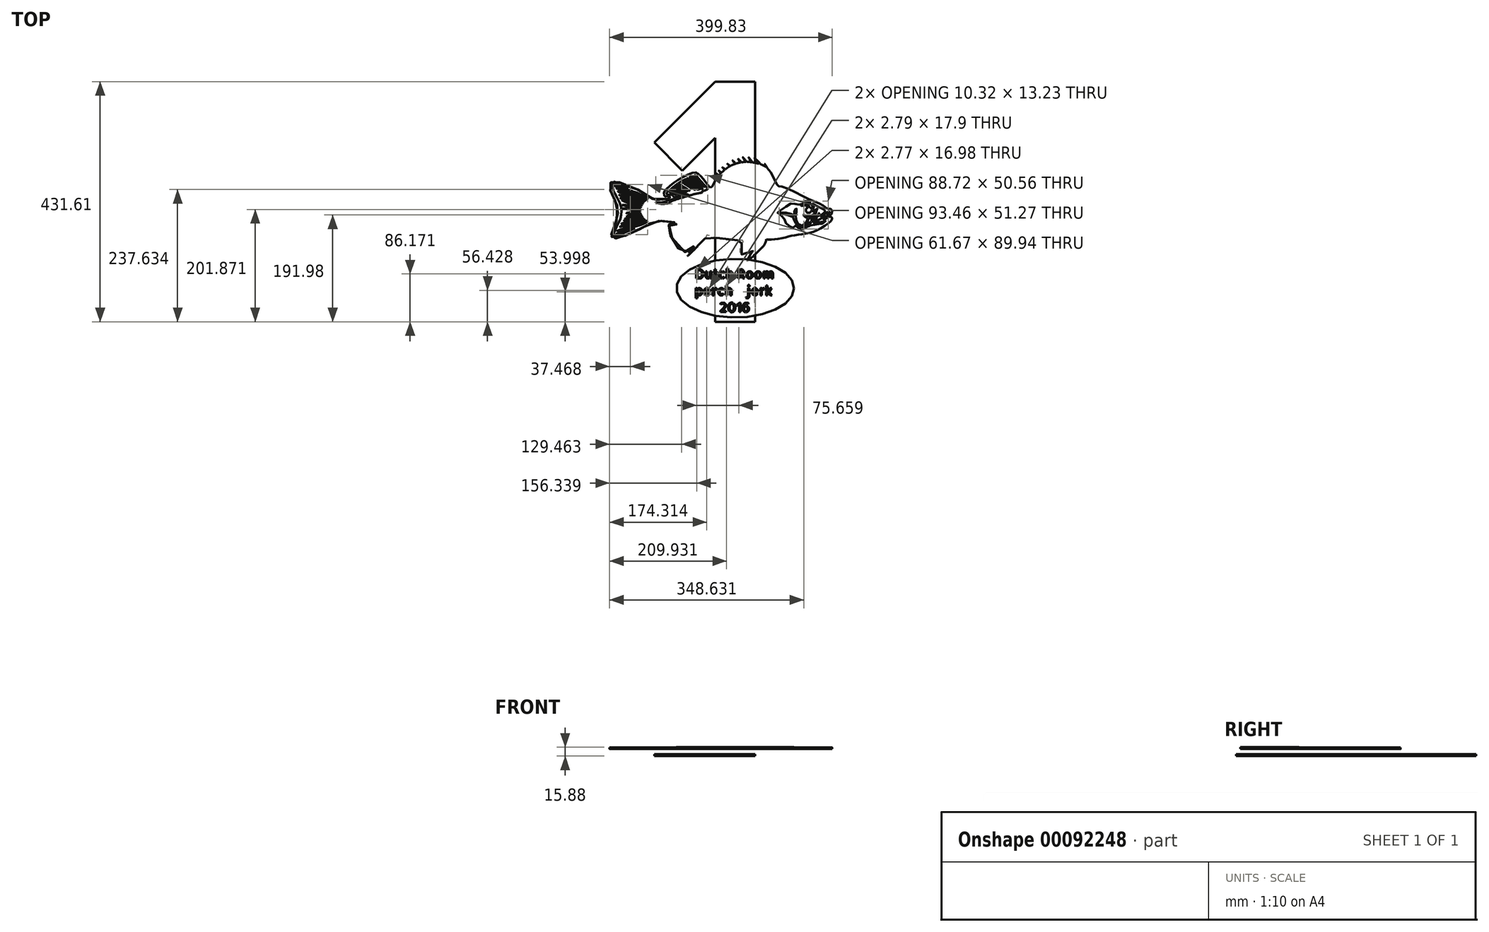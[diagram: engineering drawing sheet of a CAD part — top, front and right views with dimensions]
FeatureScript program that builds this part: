
annotation { "Feature Type Name" : "Feature", "Feature Type Description" : "" }
export const myFeature = defineFeature(function(context is Context, id is Id, definition is map)
    precondition{}
    {
        {
            var Q0;
            Q0=qCreatedBy(makeId("Top.planeOp"),FACE);
            var sketch = newSketch(context, id + "F0", { "sketchPlane" : qUnion([Q0])});
            skFitSpline(sketch, "E0", {"points": [v(176.52, -244.27) * mm, v(181.2, -242.71) * mm, v(184.05, -245.3) * mm, v(182.5, -249.99) * mm, v(166.12, -262.72) * mm, v(147.15, -271.03) * mm, v(127.92, -274.93) * mm, v(113.37, -276.75) * mm, v(102.2, -279.6) * mm, v(84.87, -283.22) * mm, v(72.52, -283.98) * mm, v(66.52, -283.55) * mm, v(66.52, -283.55) * mm], "startDerivative": vector(81.4, 45.99) * mm, "endDerivative": vector(4.56, -0.01) * mm});
            skFitSpline(sketch, "E1", {"points": [v(66.52, -283.55) * mm, v(62.28, -294) * mm, v(51.55, -305.13) * mm, v(31.43, -322.92) * mm, v(42.66, -306.88) * mm, v(44.26, -305.13) * mm, v(43.38, -303.53) * mm, v(41.05, -304.99) * mm, v(35.95, -308.05) * mm, v(30.4, -310.53) * mm, v(21.22, -310.38) * mm, v(19.47, -302.5) * mm, v(20.2, -296.53) * mm, v(22.97, -289.82) * mm, v(25.3, -288.21) * mm, v(25.16, -286.03) * mm, v(22.82, -285.44) * mm, v(2.55, -285.3) * mm, v(-21.84, -281.67) * mm, v(-40.3, -275.97) * mm, v(-41.5, -278) * mm, v(-45.18, -283.55) * mm, v(-56.84, -295.63) * mm, v(-75.03, -313) * mm, v(-64.28, -298.02) * mm, v(-63.92, -296.46) * mm, v(-65.39, -296.55) * mm, v(-71.63, -302.52) * mm, v(-78.16, -306.01) * mm, v(-86.6, -304.73) * mm, v(-102.6, -282.27) * mm, v(-109.19, -265.88) * mm, v(-108.93, -258.69) * mm, v(-107.97, -256.6) * mm, v(-94.27, -256.52) * mm, v(-93.4, -254.44) * mm, v(-105.8, -252.01) * mm, v(-114.2, -250.8) * mm, v(-131.46, -251.01) * mm, v(-145, -256.26) * mm, v(-161.4, -265.22) * mm, v(-180.4, -273.96) * mm, v(-199.85, -281.39) * mm, v(-209.53, -281.24) * mm, v(-211.93, -278.9) * mm, v(-211.33, -270.32) * mm, v(-201.79, -247.1) * mm, v(-200.61, -241.8) * mm, v(-200.76, -226.33) * mm, v(-209.59, -206.64) * mm, v(-213.82, -195.7) * mm, v(-215.13, -185.5) * mm, v(-212.5, -180.54) * mm, v(-206.96, -179.8) * mm, v(-177.94, -187.83) * mm, v(-144.11, -206.64) * mm, v(-140.17, -209.7) * mm, v(-133.8, -212.3) * mm, v(-127, -212.85) * mm, v(-113.58, -210.83) * mm], "startDerivative": vector(-201.77, -623.7) * mm, "endDerivative": vector(821.63, 283.32) * mm});
            skFitSpline(sketch, "E2", {"points": [v(-113.58, -210.83) * mm, v(-106.81, -209.28) * mm, v(-107.23, -207.02) * mm, v(-111.66, -206.3) * mm, v(-116.5, -206.5) * mm, v(-117.64, -203.3) * mm, v(-117.74, -199.7) * mm, v(-115.89, -196.3) * mm, v(-103.3, -184.43) * mm, v(-82.53, -171.12) * mm, v(-62.72, -163.46) * mm, v(-57.17, -165.44) * mm, v(-45.04, -177.42) * mm, v(-35.04, -190.1) * mm, v(-31.64, -189.07) * mm, v(-25.86, -178.35) * mm, v(-10.7, -160.5) * mm, v(5.27, -149.84) * mm, v(21.47, -145.14) * mm, v(35.7, -144.53) * mm, v(54.05, -148.13) * mm, v(67.01, -154.67) * mm, v(78, -169.98) * mm, v(87.26, -187.63) * mm, v(89.22, -188.14) * mm, v(99.74, -190.52) * mm, v(131.4, -205.68) * mm, v(139.48, -210.3) * mm, v(141.8, -211.3) * mm, v(145.18, -212.3) * mm, v(160.7, -218.96) * mm, v(162.02, -219.5) * mm, v(172.6, -225.45) * mm, v(175.46, -228.46) * mm, v(178.32, -228.46) * mm, v(181.2, -228.7) * mm, v(183.34, -230.31) * mm, v(184.58, -234.1) * mm, v(183.03, -238.58) * mm, v(176.52, -242.71) * mm, v(168.66, -248.55) * mm, v(176.52, -244.27) * mm], "startDerivative": vector(420.31, 27.33) * mm, "endDerivative": vector(492.44, 290.81) * mm});
            skFitSpline(sketch, "E3", {"points": [v(67.9, -155.44) * mm, v(63.55, -148.16) * mm, v(66.03, -153.88) * mm], "startDerivative": vector(-11.62, 20.57) * mm, "endDerivative": vector(8.42, -18.44) * mm});
            skFitSpline(sketch, "E4", {"points": [v(56.05, -148.79) * mm, v(45.15, -137.39) * mm, v(52.55, -147.68) * mm], "startDerivative": vector(-30.23, 33.1) * mm, "endDerivative": vector(24.2, -32.08) * mm});
            skFitSpline(sketch, "E5", {"points": [v(41.73, -145.27) * mm, v(34.48, -136.4) * mm, v(39.55, -144.95) * mm], "startDerivative": vector(-20.35, 26.15) * mm, "endDerivative": vector(16.4, -26.19) * mm});
            skFitSpline(sketch, "E6", {"points": [v(31.23, -144.33) * mm, v(23.93, -136.07) * mm, v(29.46, -144.35) * mm], "startDerivative": vector(-20.79, 24.67) * mm, "endDerivative": vector(17.59, -25.1) * mm});
            skFitSpline(sketch, "E7", {"points": [v(21.47, -145.14) * mm, v(15.64, -139.28) * mm, v(19.95, -145.4) * mm, v(19.97, -145.4) * mm], "startDerivative": vector(-18.77, 20.63) * mm, "endDerivative": vector(0.36, 0.58) * mm});
            skFitSpline(sketch, "E8", {"points": [v(11.32, -147.55) * mm, v(5.77, -141.8) * mm, v(10.2, -147.92) * mm], "startDerivative": vector(-16.02, 17.44) * mm, "endDerivative": vector(13.93, -18.32) * mm});
            skFitSpline(sketch, "E9", {"points": [v(0.95, -152.01) * mm, v(-3.57, -147.89) * mm, v(0, -152.56) * mm], "startDerivative": vector(-13.03, 12.6) * mm, "endDerivative": vector(11.2, -13.78) * mm});
            skFitSpline(sketch, "E10", {"points": [v(-7.5, -157.78) * mm, v(-12.5, -154.25) * mm, v(-8.76, -158.82) * mm], "startDerivative": vector(-14.36, 11.14) * mm, "endDerivative": vector(11.94, -13.32) * mm});
            skFitSpline(sketch, "E11", {"points": [v(-14.39, -163.98) * mm, v(-19.08, -160.13) * mm, v(-15.48, -165.1) * mm], "startDerivative": vector(-13.57, 12.16) * mm, "endDerivative": vector(11.37, -14.38) * mm});
            skFitSpline(sketch, "E12", {"points": [v(-19.2, -169.16) * mm, v(-23.41, -165.03) * mm, v(-20.42, -170.62) * mm], "startDerivative": vector(-12.18, 13.25) * mm, "endDerivative": vector(9.62, -15.99) * mm});
            skFitSpline(sketch, "E13", {"points": [v(-24.52, -176.18) * mm, v(-27.73, -174.74) * mm, v(-25.1, -177.07) * mm, v(-25.16, -177.17) * mm], "startDerivative": vector(-11.42, 5.96) * mm, "endDerivative": vector(-1.56, -0.68) * mm});
            skSolve(sketch);
        }
        {
            var Q0;
            Q0 = qSketchRegion(id + "F0", true);
            extrude(context, id + "F1", {"entities" : qUnion([Q0]), "depth" : 2.54 * mm});
        }
        {
            var Q0;
            Q0=qCreatedBy(makeId("Top.planeOp"),FACE);
            var sketch = newSketch(context, id + "F2", { "sketchPlane" : qUnion([Q0])});
            skFitSpline(sketch, "E14", {"points": [v(-142.26, -213.51) * mm, v(-147.05, -215.6) * mm, v(-152.07, -221.24) * mm, v(-154.16, -227.5) * mm, v(-155.38, -233.26) * mm, v(-153.8, -240.25) * mm, v(-149.87, -244.42) * mm, v(-145.45, -248.59) * mm, v(-143.73, -249.81) * mm, v(-139.32, -247.48) * mm, v(-131.23, -244.54) * mm, v(-118.23, -243.56) * mm, v(-105.72, -246.62) * mm, v(-93.21, -251.04) * mm, v(-77.15, -255.2) * mm, v(-72, -257.17) * mm, v(-75.55, -258.4) * mm, v(-61.45, -263.67) * mm, v(-42.32, -270.17) * mm, v(-22.11, -275.38) * mm, v(-3.6, -278.44) * mm, v(8.22, -280.05) * mm, v(24.12, -281.8) * mm, v(29.95, -281.94) * mm, v(30.82, -280.2) * mm, v(41.76, -276.26) * mm, v(55.9, -276.84) * mm, v(59.12, -278.59) * mm, v(47.74, -279.32) * mm, v(37.53, -281.94) * mm, v(32, -286.32) * mm, v(27.18, -292.15) * mm, v(27.32, -293.6) * mm, v(44.82, -281.8) * mm, v(46.43, -282.53) * mm, v(24.55, -298.57) * mm, v(23.82, -300.76) * mm, v(26.01, -301.05) * mm, v(33.16, -294.92) * mm, v(44.39, -286.6) * mm, v(50.8, -282.38) * mm, v(51.53, -284.13) * mm, v(48.03, -287.2) * mm, v(39.43, -293.46) * mm, v(30.53, -300.46) * mm, v(25.57, -304.55) * mm, v(31.84, -301.78) * mm, v(39.72, -295.8) * mm, v(49.64, -288.5) * mm, v(55.76, -283.84) * mm, v(56.34, -285.44) * mm, v(31.12, -304.4) * mm, v(31.7, -305.57) * mm, v(34.47, -304.55) * mm, v(54.3, -289.53) * mm, v(57.95, -285) * mm, v(57.66, -288.8) * mm, v(57.37, -291.13) * mm, v(60.43, -286.76) * mm, v(63.2, -281.36) * mm, v(64.07, -278.59) * mm, v(66.55, -279.32) * mm, v(85.51, -277.71) * mm, v(100.67, -274.05) * mm, v(108.48, -272.49) * mm, v(108.83, -270.75) * mm, v(106.22, -270.4) * mm, v(96.86, -263.47) * mm, v(90.62, -253.93) * mm, v(82.46, -243.87) * mm, v(73.62, -237.45) * mm, v(73.97, -236.07) * mm, v(80.9, -229.65) * mm, v(101.57, -216.36) * mm, v(113.84, -210.8) * mm, v(117.3, -212.43) * mm, v(122.4, -212.9) * mm, v(124.25, -210.8) * mm, v(128.88, -210.58) * mm, v(128.88, -210.58) * mm], "startDerivative": vector(-461.18, -146.1) * mm, "endDerivative": vector(-122.05, -8.96) * mm});
            skFitSpline(sketch, "E15", {"points": [v(-142.26, -213.51) * mm, v(-136.94, -215.88) * mm, v(-129.76, -217.43) * mm, v(-121.5, -217.04) * mm, v(-111.76, -214.5) * mm, v(-100.55, -210.94) * mm, v(-94.68, -209.16) * mm, v(-92.52, -208.55) * mm, v(-84.7, -206.4) * mm, v(-73.42, -203.91) * mm, v(-65.34, -202.68) * mm, v(-48.61, -199.53) * mm, v(-40.34, -198.26) * mm, v(-25.45, -194.95) * mm, v(-7.05, -192.13) * mm, v(5.6, -190.67) * mm, v(19.33, -189.7) * mm, v(36.58, -189.54) * mm, v(56.32, -187.87) * mm, v(78.33, -190.04) * mm, v(91.1, -193.47) * mm, v(101.09, -197.29) * mm, v(116.95, -203.8) * mm, v(128.88, -210.58) * mm], "startDerivative": vector(164.66, -82.1) * mm, "endDerivative": vector(236.1, -141.25) * mm});
            skFitSpline(sketch, "E16", {"points": [v(113.84, -210.8) * mm, v(108.11, -206.07) * mm, v(89.62, -200.81) * mm, v(64.5, -197.7) * mm, v(25.96, -197.7) * mm, v(-2.85, -201.4) * mm, v(-37.1, -207.43) * mm, v(-58.04, -211.88) * mm, v(-81.65, -216.02) * mm, v(-109.12, -218.96) * mm, v(-126.3, -219.23) * mm, v(-132.51, -217.05) * mm, v(-132.6, -217.04) * mm], "startDerivative": vector(-86.44, 93.94) * mm, "endDerivative": vector(-9.69, 0.28) * mm});
            skFitSpline(sketch, "E17", {"points": [v(110.88, -211.42) * mm, v(106.7, -208.35) * mm, v(100.73, -206.42) * mm, v(88.23, -204.77) * mm, v(77.85, -203.66) * mm, v(63.6, -202.47) * mm, v(62.23, -204.58) * mm, v(56.17, -228.28) * mm, v(54.6, -244.82) * mm, v(51.4, -234.07) * mm, v(48.82, -221.85) * mm, v(48.08, -202.84) * mm, v(46.61, -202.93) * mm, v(24.2, -203.48) * mm, v(23.1, -203.94) * mm, v(19.15, -224.52) * mm, v(15.75, -254.28) * mm, v(11.06, -236.28) * mm, v(9.04, -220.2) * mm, v(8.4, -206.05) * mm, v(6.1, -205.87) * mm, v(-10.71, -208.17) * mm, v(-12, -209.73) * mm, v(-16.22, -234.8) * mm, v(-18.06, -259.1) * mm, v(-24.82, -241.93) * mm, v(-28.3, -219.22) * mm, v(-28.81, -211.06) * mm, v(-29.7, -211.13) * mm, v(-47.75, -215.43) * mm, v(-48.06, -216.13) * mm, v(-49.22, -236.21) * mm, v(-49.53, -251.9) * mm, v(-54.16, -238.07) * mm, v(-57.72, -222.54) * mm, v(-58.95, -217.29) * mm, v(-60.27, -217.52) * mm, v(-81.51, -220.15) * mm, v(-82.05, -221.46) * mm, v(-82.51, -236.83) * mm, v(-83.13, -248.57) * mm, v(-88.08, -232.97) * mm, v(-90.4, -221.92) * mm, v(-91.78, -221.85) * mm, v(-101.67, -223.24) * mm, v(-111.64, -223.31) * mm, v(-111.95, -224.16) * mm, v(-112.1, -234.6) * mm, v(-112.1, -240.46) * mm, v(-115.5, -233.05) * mm, v(-118.05, -223.62) * mm, v(-130.02, -220.84) * mm, v(-131.1, -220.38) * mm, v(-135.6, -216.32) * mm, v(-135.47, -216.36) * mm], "startDerivative": vector(-300.42, 251) * mm, "endDerivative": vector(93.72, -45.72) * mm});
            skFitSpline(sketch, "E18", {"points": [v(114.07, -272.25) * mm, v(112.54, -271.02) * mm, v(112.3, -269.19) * mm, v(110.77, -268.65) * mm, v(106.68, -268.35) * mm, v(100.75, -263.87) * mm, v(94.04, -253.38) * mm, v(86.64, -242.73) * mm, v(80.42, -237.52) * mm, v(79.5, -235.96) * mm, v(80.74, -234.33) * mm, v(91.08, -226.74) * mm, v(100.89, -220.78) * mm, v(108.9, -216.64) * mm, v(115.19, -214.67) * mm, v(118.42, -215.85) * mm, v(121.55, -217.02) * mm, v(124.4, -215.8) * mm, v(126.2, -212.84) * mm, v(129.09, -212.62) * mm, v(131.99, -213.61) * mm, v(132.6, -217.15) * mm, v(134.83, -215.7) * mm, v(138.68, -214.57) * mm, v(146.58, -217.76) * mm, v(157.66, -223.72) * mm, v(171.27, -231.95) * mm, v(171.47, -234.92) * mm, v(163.96, -240.97) * mm, v(164.51, -242.66) * mm, v(172.4, -237.44) * mm, v(177.17, -234.05) * mm, v(180.4, -234.75) * mm, v(177.65, -237.77) * mm, v(166.02, -245.76) * mm, v(153.23, -252.99) * mm, v(160.84, -252.94) * mm, v(169.34, -251.6) * mm, v(172.74, -251.02) * mm, v(167.8, -254.76) * mm, v(163.1, -256.48) * mm, v(155.54, -256.22) * mm, v(152.25, -257.37) * mm, v(145.11, -258.38) * mm, v(139.47, -261) * mm, v(133.94, -264.72) * mm, v(125.11, -265.22) * mm, v(122.47, -260.9) * mm, v(118.83, -258.43) * mm, v(114.86, -261.9) * mm, v(112.32, -263.71) * mm, v(105.55, -258.02) * mm, v(100.44, -253.03) * mm, v(98.75, -247.82) * mm, v(95.06, -242.4) * mm, v(87.19, -236.87) * mm, v(86.44, -235.25) * mm, v(93.42, -230.2) * mm, v(104.62, -223.1) * mm, v(113.26, -218.38) * mm, v(119.83, -221.1) * mm, v(124.77, -221.12) * mm, v(126.68, -219.6) * mm, v(132.7, -219.83) * mm, v(134.89, -215.98) * mm, v(134.87, -215.68) * mm], "startDerivative": vector(-231.95, 104.03) * mm, "endDerivative": vector(-1.9, 17.59) * mm});
            skFitSpline(sketch, "E19", {"points": [v(114.07, -272.25) * mm, v(114.93, -272.67) * mm, v(119.04, -271.33) * mm, v(128.15, -270.86) * mm, v(136.88, -269) * mm, v(150.03, -264.7) * mm, v(156.6, -261.53) * mm, v(160.18, -259.5) * mm, v(161.11, -258.14) * mm, v(157.26, -257.94) * mm, v(152.96, -259.12) * mm, v(146.58, -260.36) * mm, v(141.2, -262.76) * mm, v(136, -266.4) * mm, v(130.3, -267.74) * mm, v(124.31, -267.9) * mm, v(121.19, -264.25) * mm, v(119.46, -262.11) * mm, v(116.13, -265.4) * mm, v(111.7, -266.3) * mm, v(105.97, -262.09) * mm, v(99.28, -255.48) * mm, v(94.25, -246.72) * mm, v(89.25, -241.55) * mm, v(83.67, -237.6) * mm, v(84.09, -232.91) * mm], "startDerivative": vector(42.63, -35.7) * mm, "endDerivative": vector(113.94, 375.94) * mm});
            skFitSpline(sketch, "E20", {"points": [v(132.56, -217.1) * mm, v(131.6, -218.46) * mm, v(129.07, -218.1) * mm, v(123.9, -218.23) * mm, v(122.18, -218.96) * mm, v(119.76, -217.82) * mm, v(114.98, -217.06) * mm, v(108.79, -218.09) * mm, v(94.64, -226.9) * mm, v(83.97, -233.3) * mm], "startDerivative": vector(-6.58, -27.36) * mm, "endDerivative": vector(-52.9, -37.16) * mm});
            skLineSegment(sketch, "E21", {"start": v(134.89, -215.85) * mm, "end": v(134.83, -215.7) * mm});
            skFitSpline(sketch, "E22", {"points": [v(89.01, -236.2) * mm, v(100.1, -235.35) * mm, v(110.68, -238.2) * mm, v(116.19, -240.38) * mm, v(116.53, -233.6) * mm, v(117.93, -230.64) * mm, v(119.7, -227.07) * mm, v(120.96, -231.7) * mm, v(119.89, -235.19) * mm, v(119.49, -247.44) * mm, v(121.59, -253.51) * mm, v(126.76, -258.11) * mm, v(136.63, -257.82) * mm, v(144.56, -252.99) * mm, v(147.04, -251.16) * mm, v(145.47, -255.27) * mm, v(136.9, -260.6) * mm, v(126.26, -261.82) * mm, v(120.4, -256.5) * mm, v(116.06, -249.48) * mm, v(115.1, -244.9) * mm, v(108.08, -241.12) * mm, v(89.01, -236.2) * mm]});
            skFitSpline(sketch, "E23", {"points": [v(157.78, -228.5) * mm, v(154.47, -230.65) * mm, v(149.76, -230.13) * mm, v(140.29, -222.43) * mm, v(136.57, -220.9) * mm, v(131.99, -221.35) * mm, v(128.16, -222.52) * mm, v(130.12, -223.42) * mm, v(131.99, -223.1) * mm, v(136.14, -222.55) * mm, v(140.13, -225.75) * mm, v(145.4, -230.7) * mm, v(149.23, -232.79) * mm, v(152.45, -234.07) * mm, v(156.41, -231.85) * mm, v(157.78, -228.5) * mm]});
            skFitSpline(sketch, "E24", {"points": [v(151.33, -233.85) * mm, v(150.28, -234.18) * mm, v(149.56, -235.95) * mm, v(146.68, -238.41) * mm, v(142.24, -239.42) * mm, v(136.75, -238.8) * mm, v(133.5, -235.2) * mm, v(132.17, -230.35) * mm, v(132.9, -225.97) * mm, v(135.58, -222.47) * mm, v(135.58, -222.47) * mm], "startDerivative": vector(-20.32, -2.1) * mm, "endDerivative": vector(-2.43, -0.54) * mm});
            skFitSpline(sketch, "E25", {"points": [v(141.16, -226.87) * mm, v(140.03, -227.18) * mm, v(137.78, -228.86) * mm, v(137.78, -232.86) * mm, v(139.73, -235.52) * mm, v(144.64, -235.33) * mm, v(147.14, -231.74) * mm], "startDerivative": vector(-10.06, -2.2) * mm, "endDerivative": vector(9.28, 22.22) * mm});
            skFitSpline(sketch, "E26", {"points": [v(151.83, -238.53) * mm, v(148.99, -241.91) * mm, v(144.24, -245.3) * mm, v(138.46, -244.7) * mm, v(134.2, -241.7) * mm, v(132.9, -239.34) * mm, v(136.54, -240.92) * mm, v(139.8, -242.05) * mm, v(145.35, -242) * mm, v(148.24, -240.02) * mm, v(151.83, -238.53) * mm]});
            skFitSpline(sketch, "E27", {"points": [v(160.82, -236.26) * mm, v(159.79, -238.66) * mm, v(157.66, -240.24) * mm, v(153.8, -242.41) * mm, v(148.46, -244.91) * mm, v(147.27, -248.12) * mm, v(147.83, -249.95) * mm, v(148.52, -247.2) * mm, v(151.68, -245.02) * mm, v(158.31, -242.21) * mm, v(161.2, -240.38) * mm, v(160.82, -236.26) * mm]});
            skFitSpline(sketch, "E28", {"points": [v(148.96, -219.04) * mm, v(149.85, -220.95) * mm, v(151.94, -223.46) * mm, v(150.6, -223.62) * mm, v(148.3, -221.75) * mm, v(144.87, -220.21) * mm, v(141.04, -220.46) * mm, v(138.77, -218.1) * mm, v(143.68, -218.1) * mm, v(146.3, -217.61) * mm], "startDerivative": vector(5.22, -18.68) * mm, "endDerivative": vector(19.33, 6.7) * mm});
            skFitSpline(sketch, "E29", {"points": [v(138.77, -224.27) * mm, v(136.97, -224.53) * mm, v(134.9, -225.82) * mm, v(134.1, -229.7) * mm, v(135.2, -234.72) * mm, v(138.5, -237.13) * mm, v(143.91, -237.4) * mm, v(147.52, -236.36) * mm, v(148.35, -234.58) * mm, v(149.23, -232.79) * mm], "startDerivative": vector(-20.93, -1.63) * mm, "endDerivative": vector(11.28, 20.03) * mm});
            skFitSpline(sketch, "E30.0.0", {"points": [v(66.52, -283.55) * mm, v(66.52, -283.55) * mm, v(66.42, -283.55) * mm, v(74.1, -284.32) * mm, v(84.7, -283.6) * mm, v(102.41, -279.81) * mm, v(113.23, -276.26) * mm, v(128.3, -275.22) * mm, v(147.76, -271.61) * mm, v(165.7, -264.01) * mm, v(182.85, -251.2) * mm, v(184.98, -245.38) * mm, v(181.16, -241.65) * mm, v(178.13, -243.36) * mm, v(176.52, -244.27) * mm]});
            skFitSpline(sketch, "E30.0.1", {"points": [v(176.52, -244.27) * mm, v(172.56, -246.6) * mm, v(164.49, -251.37) * mm, v(177.06, -241.76) * mm, v(183.4, -239.52) * mm, v(185.1, -234.14) * mm, v(183.64, -230.17) * mm, v(181.27, -228.43) * mm, v(178.38, -228.33) * mm, v(174.9, -229.08) * mm, v(173.51, -224.74) * mm, v(161.63, -219.27) * mm, v(161.13, -219.21) * mm, v(144.96, -211.84) * mm, v(141.99, -211.46) * mm, v(138.96, -210.15) * mm, v(130.98, -205.12) * mm, v(100.96, -189.67) * mm, v(89.55, -187.92) * mm, v(86.36, -188.53) * mm, v(78.01, -168.4) * mm, v(68.21, -153.75) * mm, v(54.28, -147.55) * mm, v(35.6, -143.82) * mm, v(21.51, -144.63) * mm, v(4.44, -149.08) * mm, v(-11.16, -159.71) * mm, v(-26.53, -176.94) * mm, v(-30.53, -189.27) * mm, v(-36.2, -191.76) * mm, v(-44.45, -176.23) * mm, v(-56.8, -165.31) * mm, v(-62.88, -161.88) * mm, v(-84.09, -171.24) * mm, v(-102.65, -182.95) * mm, v(-115.87, -195.67) * mm, v(-118.07, -199.5) * mm, v(-117.66, -203.16) * mm, v(-117.16, -207.63) * mm, v(-111.64, -205.96) * mm, v(-106.9, -206.24) * mm, v(-105.93, -210.33) * mm, v(-110.6, -210.64) * mm, v(-113.58, -210.83) * mm]});
            skFitSpline(sketch, "E30.0.2", {"points": [v(-113.58, -210.83) * mm, v(-118.9, -212.67) * mm, v(-126.66, -212.92) * mm, v(-133.56, -212.81) * mm, v(-140.73, -209.79) * mm, v(-144.08, -205.9) * mm, v(-177.46, -185.5) * mm, v(-205.73, -179.4) * mm, v(-212.84, -179.67) * mm, v(-216.15, -185.72) * mm, v(-213.9, -196.33) * mm, v(-210.09, -206.96) * mm, v(-198.52, -225.17) * mm, v(-200.7, -242.08) * mm, v(-201.08, -246.91) * mm, v(-212.46, -269.82) * mm, v(-212.67, -278.83) * mm, v(-209.51, -282) * mm, v(-198.67, -282.4) * mm, v(-180.05, -273.65) * mm, v(-161.56, -265.8) * mm, v(-145.06, -256.06) * mm, v(-132.35, -249.8) * mm, v(-113.65, -250.47) * mm, v(-107.06, -252.21) * mm, v(-92.07, -252.92) * mm, v(-93.81, -258.37) * mm, v(-109.08, -255.08) * mm, v(-108.76, -259.03) * mm, v(-110.28, -267.02) * mm, v(-103, -282.17) * mm, v(-88.71, -306.96) * mm, v(-78.02, -306.53) * mm, v(-71.52, -303.33) * mm, v(-66.03, -296.1) * mm, v(-63.61, -296.31) * mm, v(-63.8, -298.28) * mm, v(-84.83, -324.13) * mm, v(-54.86, -293.49) * mm, v(-45.8, -284.73) * mm, v(-41.23, -278.42) * mm, v(-40.99, -273.87) * mm, v(-19.72, -283.8) * mm, v(0.59, -285.64) * mm, v(22.16, -285.4) * mm, v(25.4, -285.47) * mm, v(25.82, -288.8) * mm, v(22.14, -289.2) * mm, v(19.9, -296.97) * mm, v(19.38, -302) * mm, v(19.27, -312.7) * mm, v(30.96, -310.86) * mm, v(35.68, -308.13) * mm, v(40.93, -305.49) * mm, v(43.4, -302.59) * mm, v(44.7, -305.65) * mm, v(42.36, -306) * mm, v(21.33, -335.07) * mm, v(53.37, -302.82) * mm, v(62.66, -295.5) * mm, v(65.33, -287.24) * mm, v(66.52, -283.55) * mm]});
            skFitSpline(sketch, "E31", {"points": [v(-73.42, -203.91) * mm, v(-77.32, -202.4) * mm, v(-91.25, -205.23) * mm, v(-99.63, -207.85) * mm, v(-100.8, -205.74) * mm, v(-105.08, -203.47) * mm, v(-110.88, -203.23) * mm, v(-111.84, -203.08) * mm, v(-112.5, -201.81) * mm, v(-112.45, -199.8) * mm, v(-107.45, -194.7) * mm, v(-94.38, -184.27) * mm, v(-79.07, -175.46) * mm, v(-65.97, -169.49) * mm, v(-62.72, -168.43) * mm, v(-60.71, -168.53) * mm, v(-58.4, -170.64) * mm, v(-52.96, -177.03) * mm, v(-44.16, -187) * mm, v(-40.17, -191.07) * mm, v(-39, -192.98) * mm, v(-45.1, -195.8) * mm, v(-49.53, -197.9) * mm, v(-38.39, -195.17) * mm, v(-29.16, -193.18) * mm, v(-22.55, -192.13) * mm, v(-10.92, -191.6) * mm, v(-6.8, -190.98) * mm, v(-14.63, -190.32) * mm, v(-22.67, -189.35) * mm, v(-23.26, -186.5) * mm, v(-21.95, -182.3) * mm, v(-11.9, -168.64) * mm, v(8.97, -152.84) * mm, v(22.45, -148.52) * mm, v(41.84, -148.93) * mm, v(57.65, -154.18) * mm, v(68.71, -162) * mm, v(77.62, -176.98) * mm, v(80.98, -186.23) * mm, v(80.13, -187) * mm, v(76.55, -186.63) * mm, v(64.72, -186.3) * mm, v(56.32, -187.87) * mm], "startDerivative": vector(-184.73, 115.27) * mm, "endDerivative": vector(-313.03, -80.23) * mm});
            skFitSpline(sketch, "E32", {"points": [v(-44.69, -269.38) * mm, v(-46.88, -269.88) * mm, v(-47.32, -272.1) * mm, v(-44.5, -272.85) * mm, v(-44.36, -275.82) * mm, v(-48.07, -280.56) * mm, v(-50.29, -283.23) * mm, v(-51.48, -282.34) * mm, v(-50.44, -279.82) * mm, v(-49.4, -276.7) * mm, v(-54.44, -281.15) * mm, v(-64.67, -291.98) * mm, v(-76.24, -301.02) * mm, v(-82.76, -302.06) * mm, v(-89, -296.13) * mm, v(-94.63, -286.64) * mm, v(-99.07, -276.56) * mm, v(-101.45, -270.63) * mm, v(-103.82, -263.06) * mm, v(-103.52, -260.54) * mm, v(-100.4, -260.99) * mm, v(-87.8, -259.95) * mm, v(-79.5, -259.5) * mm, v(-78.02, -261.58) * mm, v(-70.3, -264.55) * mm, v(-59.19, -268.4) * mm, v(-54.77, -265.85) * mm], "startDerivative": vector(-102.65, 1.55) * mm, "endDerivative": vector(106.34, 101.9) * mm});
            skFitSpline(sketch, "E33", {"points": [v(-146.92, -210.7) * mm, v(-151.58, -214.36) * mm, v(-157.4, -222.68) * mm, v(-160.57, -233) * mm, v(-157.07, -242.32) * mm, v(-151.41, -248.98) * mm, v(-147.58, -251.3) * mm, v(-150.91, -254.14) * mm, v(-174.38, -265.46) * mm, v(-197.35, -275.11) * mm, v(-205.5, -278.1) * mm, v(-208.06, -275.61) * mm, v(-207.2, -271.12) * mm, v(-201.68, -259.47) * mm, v(-195.38, -244.63) * mm, v(-194.26, -233.3) * mm, v(-196.36, -219.72) * mm, v(-206.3, -200.26) * mm, v(-208.96, -192.99) * mm, v(-209.1, -186.4) * mm, v(-205.46, -184.73) * mm, v(-192.72, -188.93) * mm, v(-174.95, -195.37) * mm, v(-158.15, -203.76) * mm, v(-146.92, -210.7) * mm]});
            skFitSpline(sketch, "E34", {"points": [v(84.97, -246.15) * mm, v(77.95, -247.33) * mm, v(55.5, -247.46) * mm, v(40.7, -248.51) * mm, v(27.75, -251.42) * mm, v(27.75, -253.53) * mm, v(35.41, -262.65) * mm, v(44.53, -271.33) * mm, v(48.04, -270.37) * mm, v(57, -266.36) * mm, v(77.38, -264.26) * mm, v(78.5, -262.53) * mm, v(78.3, -257.48) * mm, v(80.47, -255.7) * mm, v(93.23, -258.42) * mm], "startDerivative": vector(-89.77, -22.07) * mm, "endDerivative": vector(176.4, -52.95) * mm});
            skFitSpline(sketch, "E35", {"points": [v(91.99, -256.31) * mm, v(86.9, -254.22) * mm, v(80.77, -253.72) * mm, v(79.38, -251.64) * mm, v(77.7, -254.31) * mm, v(75.03, -255.8) * mm, v(74.24, -259.76) * mm, v(73.35, -261.74) * mm, v(68.3, -261.93) * mm, v(60.08, -263.32) * mm, v(53.85, -264.3) * mm, v(47.22, -268.47) * mm, v(41.68, -263.72) * mm, v(34.75, -255) * mm, v(38.41, -252.43) * mm, v(48.5, -250.45) * mm, v(70.67, -249.96) * mm, v(82.85, -248.77) * mm, v(86.5, -247.87) * mm, v(86.43, -247.79) * mm], "startDerivative": vector(-89.8, 56.11) * mm, "endDerivative": vector(-16.22, 11) * mm});
            skFitSpline(sketch, "E36", {"points": [v(-106.21, -218.66) * mm, v(-85.66, -211.06) * mm, v(-61.46, -205.71) * mm, v(-33.97, -199.74) * mm, v(-9.93, -196.45) * mm, v(10.02, -194.87) * mm, v(38.14, -193.3) * mm, v(67.04, -194.56) * mm, v(91.4, -198.26) * mm, v(82.28, -193.3) * mm, v(50.55, -189.38) * mm, v(36.58, -189.54) * mm], "startDerivative": vector(225.94, 93.48) * mm, "endDerivative": vector(-170.42, -5.76) * mm});
            skFitSpline(sketch, "E37", {"points": [v(-65.34, -202.68) * mm, v(-72.07, -204.99) * mm, v(-103.5, -214.89) * mm, v(-109.12, -218.96) * mm], "startDerivative": vector(-19.73, -7.72) * mm, "endDerivative": vector(-15, -16.13) * mm});
            skFitSpline(sketch, "E38", {"points": [v(149.76, -230.13) * mm, v(150.85, -227.38) * mm, v(151.94, -223.46) * mm], "startDerivative": vector(2.46, 5.66) * mm, "endDerivative": vector(1.93, 7.61) * mm});
            skFitSpline(sketch, "E39", {"points": [v(147.97, -228.87) * mm, v(148.97, -226.6) * mm, v(148.3, -221.75) * mm], "startDerivative": vector(3.11, 4.83) * mm, "endDerivative": vector(-2.17, 9.13) * mm});
            skFitSpline(sketch, "E40", {"points": [v(133.42, -258.62) * mm, v(139.58, -253.43) * mm, v(142.2, -245.5) * mm, v(142.04, -245.5) * mm], "startDerivative": vector(14.49, 7.56) * mm, "endDerivative": vector(-2.8, -1.15) * mm});
            skFitSpline(sketch, "E41", {"points": [v(130.09, -258.8) * mm, v(136.2, -254.47) * mm, v(139.32, -249.28) * mm, v(140.53, -245.3) * mm], "startDerivative": vector(17.83, 9.77) * mm, "endDerivative": vector(3.51, 13.55) * mm});
            skFitSpline(sketch, "E42", {"points": [v(150.95, -239.94) * mm, v(154.75, -237.25) * mm, v(156.41, -231.85) * mm], "startDerivative": vector(9.1, 4.58) * mm, "endDerivative": vector(1.91, 11.52) * mm});
            skFitSpline(sketch, "E43", {"points": [v(155.24, -233.04) * mm, v(155.04, -234.83) * mm, v(153.83, -237.08) * mm, v(150.73, -238.71) * mm, v(150.73, -238.71) * mm], "startDerivative": vector(-0.53, -6.59) * mm, "endDerivative": vector(1.65, 0.6) * mm});
            skLineSegment(sketch, "E44.trimOffspring", {"start": v(150.73, -238.71) * mm, "end": v(150.73, -238.71) * mm});
            skFitSpline(sketch, "E45", {"points": [v(-81.28, -302.39) * mm, v(-68.57, -291.2) * mm, v(-51.39, -275.2) * mm, v(-69.36, -289.76) * mm, v(-82.76, -302.06) * mm], "startDerivative": vector(44.71, 38.8) * mm, "endDerivative": vector(-44.93, -43.46) * mm});
            skFitSpline(sketch, "E46", {"points": [v(-85.05, -300.65) * mm, v(-67.9, -284.99) * mm, v(-54.43, -271.83) * mm, v(-73.38, -286.73) * mm, v(-86.4, -299.37) * mm], "startDerivative": vector(58.26, 52.77) * mm, "endDerivative": vector(-43.4, -46.3) * mm});
            skFitSpline(sketch, "E47", {"points": [v(-88.13, -297.3) * mm, v(-71.45, -282.37) * mm, v(-57.86, -270.59) * mm, v(-74.13, -282.18) * mm, v(-89, -296.13) * mm], "startDerivative": vector(55.74, 51.6) * mm, "endDerivative": vector(-48.5, -50.9) * mm});
            skFitSpline(sketch, "E48", {"points": [v(-90.93, -293.26) * mm, v(-78.3, -282.3) * mm, v(-64.78, -270.4) * mm, v(-80.05, -281.06) * mm, v(-92.3, -291) * mm], "startDerivative": vector(42.92, 37.85) * mm, "endDerivative": vector(-41.44, -35.53) * mm});
            skFitSpline(sketch, "E49", {"points": [v(-93.55, -288.75) * mm, v(-81.17, -279.5) * mm, v(-69.27, -269.71) * mm, v(-83.92, -279) * mm, v(-94.63, -286.64) * mm], "startDerivative": vector(42.37, 31.03) * mm, "endDerivative": vector(-36.95, -27.33) * mm});
            skFitSpline(sketch, "E50", {"points": [v(-95.86, -284.05) * mm, v(-84.4, -276.5) * mm, v(-72.53, -267.38) * mm, v(-85.29, -274.65) * mm, v(-96.71, -282.14) * mm], "startDerivative": vector(39.9, 24.98) * mm, "endDerivative": vector(-38.86, -26.5) * mm});
            skFitSpline(sketch, "E51", {"points": [v(-97.92, -279.34) * mm, v(-89.59, -274.35) * mm, v(-76.98, -266.27) * mm, v(-88.03, -271.16) * mm, v(-98.56, -277.8) * mm], "startDerivative": vector(29.02, 17.48) * mm, "endDerivative": vector(-34.43, -24.49) * mm});
            skFitSpline(sketch, "E52", {"points": [v(-99.9, -274.57) * mm, v(-87.8, -268.64) * mm, v(-80.62, -264.56) * mm, v(-91.81, -268.57) * mm, v(-100.45, -273.16) * mm, v(-100.45, -273.17) * mm], "startDerivative": vector(41.2, 19.87) * mm, "endDerivative": vector(0.72, -0.63) * mm});
            skFitSpline(sketch, "E53", {"points": [v(-101.45, -270.63) * mm, v(-95.22, -268.23) * mm, v(-86.06, -263.48) * mm, v(-94.35, -266.1) * mm, v(-101.91, -269.4) * mm], "startDerivative": vector(22.34, 7.43) * mm, "endDerivative": vector(-25.45, -12.06) * mm});
            skFitSpline(sketch, "E54", {"points": [v(-102.76, -267.13) * mm, v(-97.1, -265.09) * mm, v(-91.6, -262.53) * mm, v(-98.9, -263.9) * mm, v(-103.25, -265.46) * mm], "startDerivative": vector(19.34, 6.63) * mm, "endDerivative": vector(-14.97, -6.5) * mm});
            skFitSpline(sketch, "E55.trimOffspring", {"points": [v(-44.69, -269.38) * mm, v(-46.88, -269.88) * mm, v(-47.32, -272.1) * mm, v(-44.5, -272.85) * mm, v(-44.36, -275.82) * mm, v(-48.07, -280.56) * mm, v(-50.29, -283.23) * mm, v(-51.48, -282.34) * mm, v(-50.44, -279.82) * mm, v(-49.4, -276.7) * mm, v(-54.44, -281.15) * mm, v(-64.67, -291.98) * mm, v(-76.24, -301.02) * mm, v(-82.76, -302.06) * mm, v(-89, -296.13) * mm, v(-94.63, -286.64) * mm, v(-99.07, -276.56) * mm, v(-101.45, -270.63) * mm, v(-103.82, -263.06) * mm, v(-103.52, -260.54) * mm, v(-100.4, -260.99) * mm, v(-87.8, -259.95) * mm, v(-79.5, -259.5) * mm, v(-78.02, -261.58) * mm, v(-70.3, -264.55) * mm, v(-59.19, -268.4) * mm, v(-54.77, -265.85) * mm], "startDerivative": vector(-102.65, 1.55) * mm, "endDerivative": vector(106.34, 101.9) * mm});
            skFitSpline(sketch, "E56", {"points": [v(-76.24, -301.02) * mm, v(-81.28, -302.39) * mm], "startDerivative": vector(-5.04, -1.37) * mm, "endDerivative": vector(-5.04, -1.37) * mm});
            skFitSpline(sketch, "E57", {"points": [v(-149.25, -250.13) * mm, v(-158.9, -255.17) * mm, v(-202.14, -268.52) * mm, v(-171.7, -257.46) * mm, v(-159.1, -252.9) * mm, v(-150.91, -249.28) * mm], "startDerivative": vector(-36.42, -27.4) * mm, "endDerivative": vector(63.3, 28.88) * mm});
            skFitSpline(sketch, "E58", {"points": [v(-152.78, -247.93) * mm, v(-166.3, -252.75) * mm, v(-187.37, -259.07) * mm, v(-197.12, -261.08) * mm, v(-167.33, -251.1) * mm, v(-154.2, -246.45) * mm], "startDerivative": vector(-70.76, -26.04) * mm, "endDerivative": vector(52.9, 20.09) * mm});
            skFitSpline(sketch, "E59", {"points": [v(-155.57, -244.66) * mm, v(-171.03, -250.04) * mm, v(-194.45, -255.5) * mm, v(-168.87, -247.24) * mm, v(-156.57, -243.13) * mm], "startDerivative": vector(-52.14, -21.27) * mm, "endDerivative": vector(43.7, 15.6) * mm});
            skFitSpline(sketch, "E60", {"points": [v(-157.54, -241.54) * mm, v(-167.5, -245.35) * mm, v(-189.72, -250.11) * mm, v(-170.23, -244.14) * mm, v(-158.34, -240.12) * mm], "startDerivative": vector(-34.3, -17.04) * mm, "endDerivative": vector(40.86, 15.25) * mm});
            skFitSpline(sketch, "E61", {"points": [v(-159.14, -238.5) * mm, v(-171.96, -242.13) * mm, v(-188, -246.61) * mm, v(-172.54, -240.64) * mm, v(-159.73, -237.08) * mm], "startDerivative": vector(-44.38, -12.11) * mm, "endDerivative": vector(44.91, 10.43) * mm});
            skFitSpline(sketch, "E62", {"points": [v(-160.17, -235.67) * mm, v(-184.48, -241.87) * mm, v(-170.39, -236.43) * mm, v(-160.5, -234.01) * mm], "startDerivative": vector(-89.93, -25.13) * mm, "endDerivative": vector(30.6, 5.62) * mm});
            skFitSpline(sketch, "E63", {"points": [v(-147.33, -211.55) * mm, v(-168.09, -202.14) * mm, v(-194.74, -194) * mm, v(-203.6, -191.72) * mm, v(-173.17, -203.37) * mm, v(-156.3, -210.21) * mm, v(-149.5, -213.03) * mm], "startDerivative": vector(-106.32, 53.17) * mm, "endDerivative": vector(61.86, -25.4) * mm});
            skFitSpline(sketch, "E64", {"points": [v(-151.04, -213.98) * mm, v(-174.16, -205.78) * mm, v(-200.45, -197.18) * mm, v(-179.33, -206.85) * mm, v(-162.01, -212.53) * mm, v(-153.13, -215.76) * mm], "startDerivative": vector(-87.16, 30.9) * mm, "endDerivative": vector(62.3, -24.19) * mm});
            skFitSpline(sketch, "E65", {"points": [v(-154.5, -217.46) * mm, v(-177.13, -209.82) * mm, v(-198.1, -203.93) * mm, v(-171.79, -213.84) * mm, v(-155.7, -219.38) * mm, v(-155.69, -219.35) * mm], "startDerivative": vector(-77.3, 27.53) * mm, "endDerivative": vector(2.56, 1.27) * mm});
            skFitSpline(sketch, "E66", {"points": [v(-156.5, -220.86) * mm, v(-196.02, -209.5) * mm, v(-169.6, -218.73) * mm, v(-157.4, -222.68) * mm], "startDerivative": vector(-146.45, 43.7) * mm, "endDerivative": vector(38.46, -12.12) * mm});
            skFitSpline(sketch, "E67", {"points": [v(-158.07, -224.06) * mm, v(-178.37, -218.17) * mm, v(-193.47, -213.5) * mm, v(-168.49, -223.56) * mm, v(-158.81, -225.72) * mm], "startDerivative": vector(-67.23, 18.22) * mm, "endDerivative": vector(37.01, -3.94) * mm});
            skFitSpline(sketch, "E68", {"points": [v(-160.17, -229.65) * mm, v(-176.77, -228.11) * mm, v(-192.15, -228.18) * mm, v(-176.2, -229.94) * mm, v(-160.5, -231.41) * mm], "startDerivative": vector(-56.51, 7.22) * mm, "endDerivative": vector(54.1, -5.25) * mm});
            skFitSpline(sketch, "E69", {"points": [v(-159.86, -228.54) * mm, v(-176.99, -225.42) * mm, v(-192.54, -222.02) * mm, v(-177.4, -222.69) * mm, v(-170.1, -224.44) * mm, v(-159.3, -226.92) * mm, v(-159.33, -227) * mm], "startDerivative": vector(-65.15, 12.01) * mm, "endDerivative": vector(-5.2, -4.66) * mm});
            skFitSpline(sketch, "E70", {"points": [v(-160.57, -233) * mm, v(-185.26, -236.64) * mm, v(-176.33, -234.01) * mm, v(-165.99, -232.38) * mm, v(-160.55, -232.07) * mm], "startDerivative": vector(-101.72, -17.26) * mm, "endDerivative": vector(30.09, 1.18) * mm});
            skFitSpline(sketch, "E71", {"points": [v(-169.83, -263.46) * mm, v(-186.33, -268.62) * mm, v(-203.8, -274.1) * mm, v(-182.72, -265.39) * mm, v(-154.72, -256.18) * mm, v(-154.78, -256.22) * mm], "startDerivative": vector(-64.65, -20.13) * mm, "endDerivative": vector(-7.06, -3.1) * mm});
            skFitSpline(sketch, "E72", {"points": [v(-164.23, -200.66) * mm, v(-181.6, -194.75) * mm, v(-205.02, -188.4) * mm, v(-181.66, -192.8) * mm], "startDerivative": vector(-46.22, 17.82) * mm, "endDerivative": vector(104, -21.04) * mm});
            skFitSpline(sketch, "E73", {"points": [v(-63.2, -168.53) * mm, v(-53.7, -178.6) * mm, v(-44.18, -189.44) * mm, v(-59.68, -175.99) * mm, v(-65.97, -169.49) * mm], "startDerivative": vector(32.45, -34.13) * mm, "endDerivative": vector(-21.46, 24.35) * mm});
            skFitSpline(sketch, "E74", {"points": [v(-68.2, -170.42) * mm, v(-57.48, -180.27) * mm, v(-47.1, -189.77) * mm, v(-62.6, -178.5) * mm, v(-70.23, -171.31) * mm], "startDerivative": vector(36.04, -34.04) * mm, "endDerivative": vector(-25.32, 27.25) * mm});
            skFitSpline(sketch, "E75", {"points": [v(-72.83, -172.5) * mm, v(-60.6, -182.25) * mm, v(-48.43, -193.44) * mm, v(-65.53, -181.1) * mm, v(-74.94, -173.47) * mm], "startDerivative": vector(42.67, -32.42) * mm, "endDerivative": vector(-32.52, 27.5) * mm});
            skFitSpline(sketch, "E76", {"points": [v(-77.19, -174.54) * mm, v(-65.53, -183.22) * mm, v(-52.83, -193.53) * mm, v(-70.47, -181.9) * mm, v(-79.07, -175.46) * mm], "startDerivative": vector(40.17, -29.22) * mm, "endDerivative": vector(-29.89, 23.65) * mm});
            skFitSpline(sketch, "E77", {"points": [v(-80.76, -176.3) * mm, v(-68.44, -185.16) * mm, v(-56.1, -194.68) * mm, v(-73.73, -183.66) * mm, v(-82.77, -177.33) * mm], "startDerivative": vector(42.17, -29.8) * mm, "endDerivative": vector(-31.41, 22.99) * mm});
            skFitSpline(sketch, "E78", {"points": [v(-84.5, -178.25) * mm, v(-74.09, -185.86) * mm, v(-61.48, -194.6) * mm, v(-77.96, -185.69) * mm, v(-86.47, -179.32) * mm], "startDerivative": vector(35.2, -27.25) * mm, "endDerivative": vector(-28.1, 24.66) * mm});
            skFitSpline(sketch, "E79", {"points": [v(-88.6, -180.56) * mm, v(-75.85, -188.95) * mm, v(-65.18, -196.44) * mm, v(-81.67, -187.45) * mm, v(-90.39, -181.64) * mm, v(-90.32, -181.6) * mm], "startDerivative": vector(44.34, -28.82) * mm, "endDerivative": vector(5.15, 1.26) * mm});
            skFitSpline(sketch, "E80", {"points": [v(-92.04, -182.7) * mm, v(-81.4, -189.74) * mm, v(-71.44, -196.44) * mm, v(-85.81, -189.21) * mm, v(-93.94, -183.96) * mm], "startDerivative": vector(36.03, -24.36) * mm, "endDerivative": vector(-27.5, 19.66) * mm});
            skFitSpline(sketch, "E81", {"points": [v(-95.38, -184.98) * mm, v(-87.05, -190.84) * mm, v(-75.65, -197.66) * mm, v(-90.04, -190.84) * mm, v(-96.93, -186.12) * mm], "startDerivative": vector(27.64, -21.6) * mm, "endDerivative": vector(-22.81, 18.87) * mm});
            skFitSpline(sketch, "E82", {"points": [v(-98.62, -187.4) * mm, v(-89, -194.11) * mm, v(-77.7, -198.97) * mm, v(-89.48, -195.8) * mm, v(-99.75, -188.3) * mm], "startDerivative": vector(31.04, -27.5) * mm, "endDerivative": vector(-31.65, 31.63) * mm});
            skFitSpline(sketch, "E83", {"points": [v(-101.6, -189.8) * mm, v(-93.3, -196.54) * mm, v(-82.56, -200.18) * mm, v(-92, -198.97) * mm, v(-102.77, -190.75) * mm], "startDerivative": vector(25.48, -30) * mm, "endDerivative": vector(-32.28, 35.77) * mm});
            skFitSpline(sketch, "E84", {"points": [v(-105.32, -192.89) * mm, v(-101.71, -195.82) * mm, v(-91.97, -201.7) * mm, v(-100.3, -198.73) * mm, v(-106.17, -193.61) * mm], "startDerivative": vector(11.6, -13.4) * mm, "endDerivative": vector(-16.81, 22) * mm});
            skFitSpline(sketch, "E85", {"points": [v(-108.25, -195.38) * mm, v(-104.44, -198.55) * mm, v(-95.71, -203.39) * mm, v(-103.12, -201.02) * mm, v(-109.52, -196.47) * mm], "startDerivative": vector(11.7, -15.43) * mm, "endDerivative": vector(-19.03, 20.23) * mm});
            skFitSpline(sketch, "E86", {"points": [v(78.3, -186.9) * mm, v(71, -172.65) * mm, v(61.32, -156.1) * mm], "startDerivative": vector(-14.5, 29.43) * mm, "endDerivative": vector(-19.36, 32.15) * mm});
            skFitSpline(sketch, "E87", {"points": [v(75.03, -186.46) * mm, v(65.24, -167.2) * mm, v(57.65, -154.18) * mm], "startDerivative": vector(-18.32, 37.15) * mm, "endDerivative": vector(-16.39, 27.1) * mm});
            skFitSpline(sketch, "E88", {"points": [v(71.71, -186.23) * mm, v(61.54, -168) * mm, v(54.41, -157.96) * mm, v(48.39, -150.5) * mm], "startDerivative": vector(-25.46, 47.88) * mm, "endDerivative": vector(-21.61, 26.34) * mm});
            skFitSpline(sketch, "E89", {"points": [v(67.88, -186.16) * mm, v(61.54, -173.81) * mm, v(51.64, -158.75) * mm, v(44.45, -149.46) * mm], "startDerivative": vector(-17.38, 36.45) * mm, "endDerivative": vector(-22.76, 28.46) * mm});
            skFitSpline(sketch, "E90", {"points": [v(64.72, -186.3) * mm, v(54.94, -171.7) * mm, v(46.62, -159.81) * mm, v(36.89, -148.3) * mm], "startDerivative": vector(-28.5, 42.44) * mm, "endDerivative": vector(-30.92, 35.01) * mm});
            skFitSpline(sketch, "E91", {"points": [v(61.68, -186.67) * mm, v(52.96, -174.47) * mm, v(43.31, -160.87) * mm, v(33.04, -148.07) * mm, v(33.17, -148.07) * mm], "startDerivative": vector(-28.9, 39.6) * mm, "endDerivative": vector(6.19, -2.05) * mm});
            skFitSpline(sketch, "E92", {"points": [v(58.4, -187.35) * mm, v(51.96, -178.2) * mm, v(40.61, -164.62) * mm, v(29.28, -152.88) * mm, v(25.06, -148.25) * mm], "startDerivative": vector(-24.92, 36.9) * mm, "endDerivative": vector(-20.56, 23.3) * mm});
            skFitSpline(sketch, "E93", {"points": [v(56.32, -187.87) * mm, v(49.62, -179.3) * mm, v(39.45, -167.35) * mm, v(26.55, -153.92) * mm, v(22.45, -148.52) * mm], "startDerivative": vector(-27.6, 35.83) * mm, "endDerivative": vector(-17.98, 26.43) * mm});
            skFitSpline(sketch, "E94", {"points": [v(14.3, -150.42) * mm, v(22.72, -157.87) * mm, v(33.4, -167.65) * mm, v(44.08, -179.66) * mm, v(45.26, -182.33) * mm, v(31.18, -169.28) * mm, v(15.6, -154.75) * mm, v(11.68, -151.5) * mm], "startDerivative": vector(59.44, -52.5) * mm, "endDerivative": vector(-36.16, 28.97) * mm});
            skFitSpline(sketch, "E95", {"points": [v(5.3, -154.95) * mm, v(15.3, -162.46) * mm, v(27.32, -173.58) * mm, v(34.88, -181.74) * mm, v(26.13, -176.25) * mm, v(16.35, -167.36) * mm, v(2.88, -156.5) * mm], "startDerivative": vector(62.26, -44.33) * mm, "endDerivative": vector(-76.7, 58.72) * mm});
            skFitSpline(sketch, "E96", {"points": [v(-2.77, -160.56) * mm, v(7.3, -167.06) * mm, v(20.65, -177.14) * mm, v(25.98, -183.52) * mm, v(16.64, -177.44) * mm, v(7.15, -170.03) * mm, v(-2.34, -163.2) * mm, v(-4.5, -161.92) * mm], "startDerivative": vector(62.22, -39.7) * mm, "endDerivative": vector(-24.18, 12.83) * mm});
            skFitSpline(sketch, "E97", {"points": [v(-9.19, -165.98) * mm, v(-1.6, -170.47) * mm, v(8.78, -177.44) * mm, v(16.35, -183.07) * mm, v(4.04, -177.59) * mm, v(-3.38, -172.25) * mm, v(-10.81, -167.54) * mm], "startDerivative": vector(48.06, -26.7) * mm, "endDerivative": vector(-51.35, 30.1) * mm});
            skFitSpline(sketch, "E98", {"points": [v(-14.13, -171.06) * mm, v(-4.56, -176.16) * mm, v(7.1, -184.04) * mm, v(-5.15, -179.34) * mm, v(-15.71, -172.93) * mm], "startDerivative": vector(34.15, -16.82) * mm, "endDerivative": vector(-34.8, 24.34) * mm});
            skFitSpline(sketch, "E99", {"points": [v(-19.18, -177.6) * mm, v(-12.45, -179.45) * mm, v(-5.5, -183.46) * mm, v(-11.86, -181.57) * mm, v(-17.5, -179.57) * mm, v(-20.38, -179.47) * mm], "startDerivative": vector(26.97, -4.52) * mm, "endDerivative": vector(-18.64, 3.1) * mm});
            skFitSpline(sketch, "E100", {"points": [v(-6.8, -190.98) * mm, v(-10.63, -186.49) * mm, v(-17.56, -182.53) * mm, v(-21.19, -180.85) * mm], "startDerivative": vector(-9.43, 13.96) * mm, "endDerivative": vector(-11.8, 5.4) * mm});
            skFitSpline(sketch, "E101", {"points": [v(153.23, -252.99) * mm, v(151.87, -251.63) * mm, v(153.23, -248.67) * mm, v(156.85, -246.27) * mm, v(155.5, -243.33) * mm], "startDerivative": vector(-9.08, 5.62) * mm, "endDerivative": vector(-10.01, 12.75) * mm});
            skFitSpline(sketch, "E102", {"points": [v(153.92, -244.03) * mm, v(154.82, -245) * mm, v(154.82, -246.2) * mm, v(151.7, -247.8) * mm, v(150.15, -251.58) * mm, v(152.27, -253.95) * mm, v(155.37, -253.39) * mm], "startDerivative": vector(8.75, -7.32) * mm, "endDerivative": vector(17.37, 6.73) * mm});
            skFitSpline(sketch, "E103", {"points": [v(78.3, -186.9) * mm, v(75.03, -186.46) * mm], "startDerivative": vector(-3.26, 0.47) * mm, "endDerivative": vector(-3.26, 0.47) * mm});
            skFitSpline(sketch, "E104", {"points": [v(71.71, -186.23) * mm, v(67.88, -186.16) * mm], "startDerivative": vector(-3.83, 0.06) * mm, "endDerivative": vector(-3.83, 0.06) * mm});
            skFitSpline(sketch, "E105", {"points": [v(64.72, -186.3) * mm, v(61.68, -186.67) * mm], "startDerivative": vector(-3.04, -0.38) * mm, "endDerivative": vector(-3.04, -0.38) * mm});
            skFitSpline(sketch, "E106", {"points": [v(58.4, -187.35) * mm, v(56.32, -187.87) * mm], "startDerivative": vector(-2.1, -0.53) * mm, "endDerivative": vector(-2.1, -0.53) * mm});
            skFitSpline(sketch, "E107", {"points": [v(52.59, -183.06) * mm, v(55.05, -184.32) * mm, v(54.66, -181.9) * mm, v(54.6, -181.81) * mm], "startDerivative": vector(7.15, -5.49) * mm, "endDerivative": vector(-0.48, 0.32) * mm});
            skFitSpline(sketch, "E108", {"points": [v(57.3, -180.63) * mm, v(60.63, -183.24) * mm, v(60.1, -179.43) * mm, v(60.05, -179.34) * mm], "startDerivative": vector(9.15, -10.56) * mm, "endDerivative": vector(-0.57, 0.3) * mm});
            skFitSpline(sketch, "E109", {"points": [v(65.12, -180.47) * mm, v(67.45, -181.95) * mm, v(67.31, -178.01) * mm], "startDerivative": vector(6.38, -5.62) * mm, "endDerivative": vector(-1.72, 10.08) * mm});
            skFitSpline(sketch, "E110", {"points": [v(72.75, -181.83) * mm, v(74.63, -183.12) * mm, v(75.05, -180.38) * mm], "startDerivative": vector(4.86, -4.52) * mm, "endDerivative": vector(-0.31, 7.2) * mm});
            skFitSpline(sketch, "E111", {"points": [v(45.31, -267.75) * mm, v(53.6, -262.35) * mm, v(68.5, -259.13) * mm, v(53.16, -260.58) * mm, v(44.4, -266.9) * mm], "startDerivative": vector(26.15, 26.82) * mm, "endDerivative": vector(-26.06, -31.95) * mm});
            skFitSpline(sketch, "E112", {"points": [v(43.72, -266.13) * mm, v(48.72, -260.47) * mm, v(68.1, -257.36) * mm, v(52.83, -257.24) * mm, v(43.78, -261.74) * mm, v(42.49, -264.66) * mm], "startDerivative": vector(12.5, 37.44) * mm, "endDerivative": vector(-7.96, -26.05) * mm});
            skFitSpline(sketch, "E113", {"points": [v(40.8, -262.77) * mm, v(44.44, -258.63) * mm, v(55.92, -255.07) * mm, v(71.86, -255.41) * mm, v(60.58, -253.39) * mm, v(43.24, -256.94) * mm, v(39.49, -261.4) * mm], "startDerivative": vector(26.9, 37.46) * mm, "endDerivative": vector(-51.25, -48.85) * mm});
            skFitSpline(sketch, "E114", {"points": [v(37.38, -259.21) * mm, v(42.12, -255.56) * mm, v(49.84, -252.6) * mm, v(75.17, -252.8) * mm, v(63.54, -251.26) * mm, v(46.67, -251.9) * mm, v(44.1, -252.74) * mm, v(39.64, -255.46) * mm, v(36.58, -258.32) * mm], "startDerivative": vector(47.58, 36.75) * mm, "endDerivative": vector(-31.58, -33.26) * mm});
            skFitSpline(sketch, "E115", {"points": [v(-49.53, -197.9) * mm, v(-50.26, -198.82) * mm, v(-48.61, -199.53) * mm], "startDerivative": vector(-2.74, -2.22) * mm, "endDerivative": vector(4.28, -1.08) * mm});
            skFitSpline(sketch, "E116", {"points": [v(-6.8, -190.98) * mm, v(-6.13, -191.38) * mm, v(-7.05, -192.13) * mm], "startDerivative": vector(2.28, -0.77) * mm, "endDerivative": vector(-2.57, -1.5) * mm});
            skSolve(sketch);
        }
        {
            var Q0;
            {var subQ4=sQuery(id+"F2.wireOp",EDGE,"E14");Q0=makeQuery(id+"F2.imprint","IMPRINT",FACE,{"disambiguationData":[TD([[makeQuery(id+"F2.imprint","IMPRINT",EDGE,{"derivedFrom":subQ4}),1.0]])]});}
            var Q1;
            {var subQ0=sQuery(id+"F2.wireOp",EDGE,"E14");var subQ1=sQuery(id+"F2.wireOp",EDGE,"E35");var subQ2=makeQuery(id+"F2.imprint","INTERSECT",VERTEX,{"disambiguationData":[OD(0.0)],"derivedFrom":[subQ1,subQ0]});Q1=makeQuery(id+"F2.imprint","IMPRINT",FACE,{"disambiguationData":[TD([[makeQuery(id+"F2.imprint","IMPRINT",EDGE,{"disambiguationData":[TD([[subQ2,-1.0]])],"derivedFrom":subQ1}),-1.0]])]});}
            var Q2;
            Q2=makeQuery(id+"F2.imprint","IMPRINT",FACE,{"disambiguationData":[TD([[makeQuery(id+"F2.imprint","IMPRINT",EDGE,{"derivedFrom":sQuery(id+"F2.wireOp",EDGE,"E21")}),-1.0]])]});
            var Q3;
            Q3=makeQuery(id+"F2.imprint","IMPRINT",FACE,{"disambiguationData":[TD([[makeQuery(id+"F2.imprint","IMPRINT",EDGE,{"derivedFrom":sQuery(id+"F2.wireOp",EDGE,"E16")}),-1.0]])]});
            var Q4;
            Q4=makeQuery(id+"F2.imprint","IMPRINT",FACE,{"disambiguationData":[TD([[makeQuery(id+"F2.imprint","IMPRINT",EDGE,{"derivedFrom":sQuery(id+"F2.wireOp",EDGE,"E33")}),-1.0]])]});
            var Q5;
            Q5=makeQuery(id+"F2.imprint","IMPRINT",FACE,{"disambiguationData":[TD([[makeQuery(id+"F2.imprint","IMPRINT",EDGE,{"derivedFrom":sQuery(id+"F2.wireOp",EDGE,"E18")}),-1.0]])]});
            var Q6;
            Q6=makeQuery(id+"F2.imprint","IMPRINT",FACE,{"disambiguationData":[TD([[makeQuery(id+"F2.imprint","IMPRINT",EDGE,{"derivedFrom":sQuery(id+"F2.wireOp",EDGE,"E25")}),-1.0]])]});
            extrude(context, id + "F3", {"entities" : qUnion([Q0, Q1, Q2, Q3, Q4, Q5, Q6]), "depth" : 25.4 * mm});
        }
        {
            var Q0;
            Q0=makeQuery(id+"F2.imprint","IMPRINT",FACE,{"disambiguationData":[TD([[makeQuery(id+"F2.imprint","IMPRINT",EDGE,{"derivedFrom":sQuery(id+"F2.wireOp",EDGE,"E21")}),-1.0]])]});
            var Q1;
            Q1=makeQuery(id+"F2.imprint","IMPRINT",FACE,{"disambiguationData":[TD([[makeQuery(id+"F2.imprint","IMPRINT",EDGE,{"derivedFrom":sQuery(id+"F2.wireOp",EDGE,"E18")}),-1.0]])]});
            var Q2;
            {var subQ0=sQuery(id+"F2.wireOp",EDGE,"E14");Q2=makeQuery(id+"F2.imprint","IMPRINT",FACE,{"disambiguationData":[TD([[makeQuery(id+"F2.imprint","IMPRINT",EDGE,{"derivedFrom":subQ0}),1.0]])]});}
            var Q3;
            {var subQ0=sQuery(id+"F2.wireOp",EDGE,"E14");var subQ1=sQuery(id+"F2.wireOp",EDGE,"E35");var subQ2=makeQuery(id+"F2.imprint","INTERSECT",VERTEX,{"disambiguationData":[OD(0.0)],"derivedFrom":[subQ1,subQ0]});Q3=makeQuery(id+"F2.imprint","IMPRINT",FACE,{"disambiguationData":[TD([[makeQuery(id+"F2.imprint","IMPRINT",EDGE,{"disambiguationData":[TD([[subQ2,-1.0]])],"derivedFrom":subQ1}),-1.0]])]});}
            var Q4;
            Q4=makeQuery(id+"F2.imprint","IMPRINT",FACE,{"disambiguationData":[TD([[makeQuery(id+"F2.imprint","IMPRINT",EDGE,{"derivedFrom":sQuery(id+"F2.wireOp",EDGE,"E16")}),-1.0]])]});
            var Q5;
            Q5=makeQuery(id+"F2.imprint","IMPRINT",FACE,{"disambiguationData":[TD([[makeQuery(id+"F2.imprint","IMPRINT",EDGE,{"derivedFrom":sQuery(id+"F2.wireOp",EDGE,"E33")}),-1.0]])]});
            var Q6;
            Q6=makeQuery(id+"F2.imprint","IMPRINT",FACE,{"disambiguationData":[TD([[makeQuery(id+"F2.imprint","IMPRINT",EDGE,{"derivedFrom":sQuery(id+"F2.wireOp",EDGE,"E25")}),-1.0]])]});
            var Q7;
            {var subQ2=sQuery(id+"F2.wireOp",EDGE,"E31");Q7=makeQuery(id+"F2.imprint","IMPRINT",FACE,{"disambiguationData":[TD([[makeQuery(id+"F2.imprint","IMPRINT",EDGE,{"derivedFrom":subQ2}),-1.0]])]});}
            extrude(context, id + "F4", {"entities" : qUnion([Q0, Q1, Q2, Q3, Q4, Q5, Q6, Q7]), "operationType" : NewBodyOperationType.REMOVE, "endBound" : BoundingType.THROUGH_ALL, "depth" : 3.17 * mm});
        }
        {
            var Q0;
            Q0=qCreatedBy(makeId("Top.planeOp"),FACE);
            cPlane(context, id + "F5", {"entities" : qUnion([Q0]), "cplaneType" : CPlaneType.OFFSET, "offset" : 12.7 * mm, "oppositeDirection" : true, "width" : 152.4 * mm, "height" : 152.4 * mm});
        }
        {
            var Q0;
            Q0=qCreatedBy(id+"F5.planeOp",FACE);
            var sketch = newSketch(context, id + "F6", { "sketchPlane" : qUnion([Q0])});
            skText(sketch, "E117", { "text": "1", "fontName": "AllertaStencil-Regular.ttf"});
            const initialGuessF6  = {"E117": [-0.15193, -0.4318, 1, 0, 0.4318]};
            skSetInitialGuess(sketch, initialGuessF6);
            skSolve(sketch);
        }
        {
            var Q0;
            Q0 = qSketchRegion(id + "F6", true);
            extrude(context, id + "F7", {"entities" : qUnion([Q0]), "depth" : 3.17 * mm});
        }
        {
            var Q0;
            Q0=qCreatedBy(makeId("Top.planeOp"),FACE);
            var sketch = newSketch(context, id + "F8", { "sketchPlane" : qUnion([Q0])});
            skText(sketch, "E118", { "text": "                          Dutch Room \n                          perch    jerk\n                                 2016", "fontName": "AllertaStencil-Regular.ttf"});
            skEllipse(sketch, "E119", {"center": v(10.32, -371.42) * mm, "majorRadius": 105.64 * mm, "minorRadius": 52.74 * mm, "majorAxis": v(1, 0)});
            skLineSegment(sketch, "E120.0", {"start": v(46.07, -431.8) * mm, "end": v(-25.43, -431.8) * mm, "construction": true});
            skPoint(sketch, "E121", {"position": v(10.32, -431.8) * mm});
            const initialGuessF8  = {"E118": [-0.22672, -0.35412, 1, 0, 0.01699]};
            skSetInitialGuess(sketch, initialGuessF8);
            skSolve(sketch);
        }
        {
            var Q0;
            Q0 = qSketchRegion(id + "F8", true);
            extrude(context, id + "F9", {"entities" : qUnion([Q0]), "depth" : 3.17 * mm});
        }
    });
